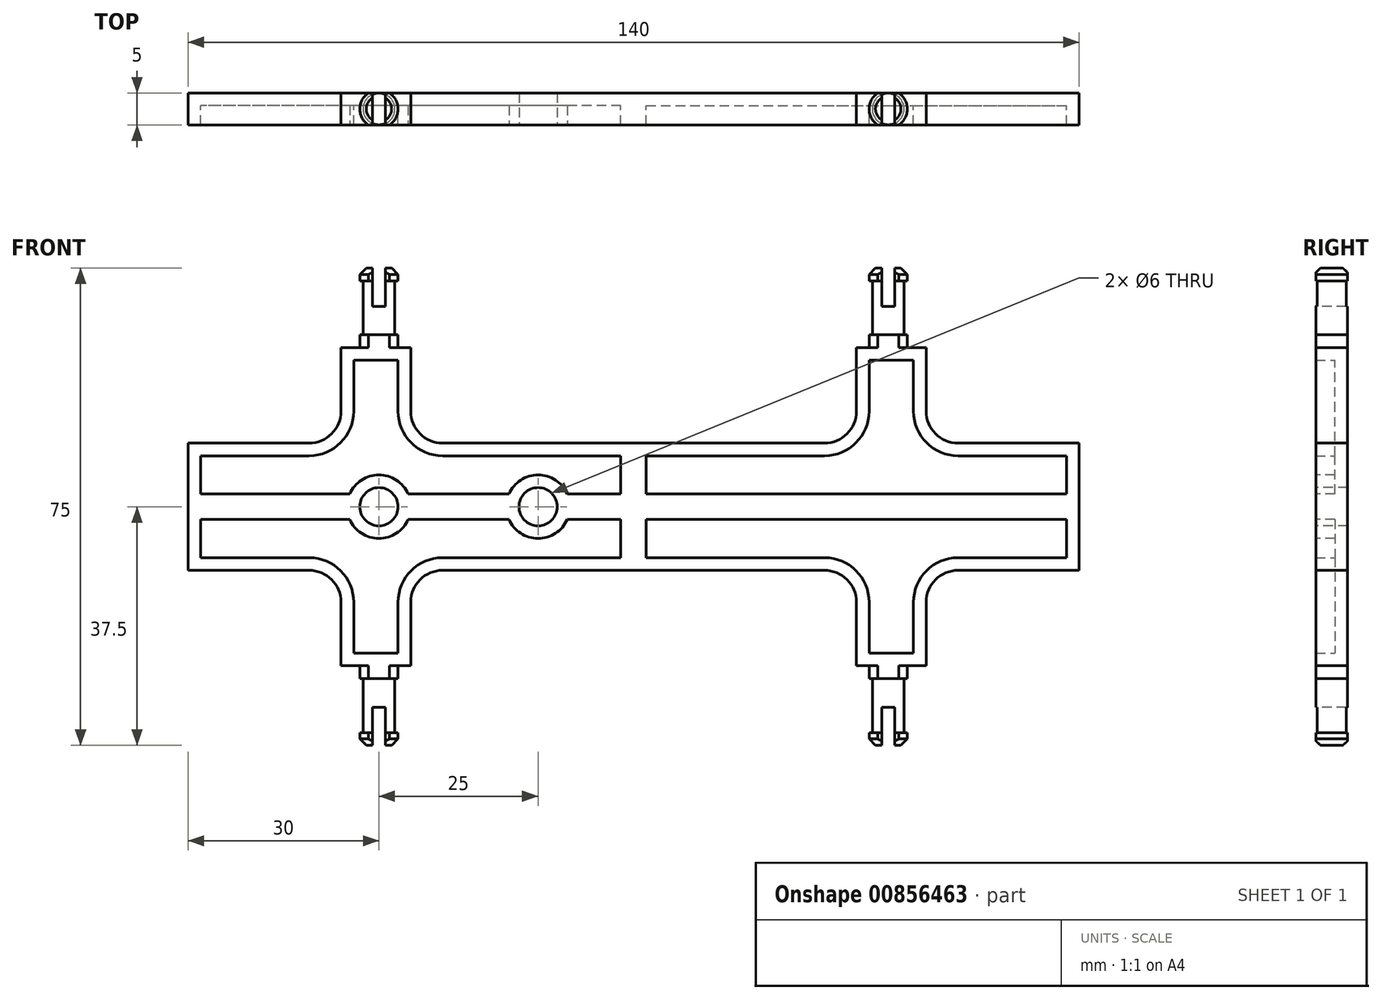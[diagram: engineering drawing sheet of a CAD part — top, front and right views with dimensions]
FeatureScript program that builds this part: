
annotation { "Feature Type Name" : "Feature", "Feature Type Description" : "" }
export const myFeature = defineFeature(function(context is Context, id is Id, definition is map)
    precondition{}
    {
        {
            var Q0;
            Q0=qCreatedBy(makeId("Front.planeOp"),FACE);
            var sketch = newSketch(context, id + "F0", { "sketchPlane" : qUnion([Q0])});
            skLineSegment(sketch, "E0.bottom", {"start": v(0, 0) * mm, "end": v(70, 0) * mm});
            skLineSegment(sketch, "E0.top", {"start": v(0, 10) * mm, "end": v(30, 10) * mm});
            skLineSegment(sketch, "E0.left", {"start": v(0, 0) * mm, "end": v(0, 10) * mm});
            skLineSegment(sketch, "E0.right", {"start": v(70, 0) * mm, "end": v(70, 10) * mm});
            skLineSegment(sketch, "E1.top", {"start": v(35, 25) * mm, "end": v(45.97, 25) * mm});
            skLineSegment(sketch, "E1.left", {"start": v(35, 15) * mm, "end": v(35, 25) * mm});
            skLineSegment(sketch, "E1.right", {"start": v(45.97, 15) * mm, "end": v(45.97, 25) * mm});
            skLineSegment(sketch, "E2.trimOffspring", {"start": v(50.97, 10) * mm, "end": v(70, 10) * mm});
            skPoint(sketch, "E3.visualSharp", {"position": v(35, 10) * mm});
            skArc(sketch, "E3.filletArc", {"start": v(30, 10) * mm, "mid": v(33.54, 11.46) * mm, "end": v(35, 15) * mm});
            skPoint(sketch, "E4.visualSharp", {"position": v(45.97, 10) * mm});
            skArc(sketch, "E4.filletArc", {"start": v(45.97, 15) * mm, "mid": v(47.43, 11.46) * mm, "end": v(50.97, 10) * mm});
            skSolve(sketch);
        }
        {
            var Q0;
            Q0 = qSketchRegion(id + "F0", true);
            extrude(context, id + "F1", {"entities" : qUnion([Q0]), "endBound" : BoundingType.SYMMETRIC, "depth" : 5 * mm, "offsetDistance" : 25 * mm});
        }
        {
            var Q0;
            Q0=makeQuery(id+"F1.opExtrude","CAP_FACE",FACE,{"disambiguationData":[OSD([sQuery(id+"F0.wireOp",EDGE,"E0.bottom"),sQuery(id+"F0.wireOp",EDGE,"E0.top"),sQuery(id+"F0.wireOp",EDGE,"E0.left"),sQuery(id+"F0.wireOp",EDGE,"E0.right"),sQuery(id+"F0.wireOp",EDGE,"E1.top"),sQuery(id+"F0.wireOp",EDGE,"E1.left"),sQuery(id+"F0.wireOp",EDGE,"E1.right"),sQuery(id+"F0.wireOp",EDGE,"E2.trimOffspring"),sQuery(id+"F0.wireOp",EDGE,"E3.filletArc"),sQuery(id+"F0.wireOp",EDGE,"E4.filletArc")])],"isStart":false});
            shell(context, id + "F2", {"entities" : qUnion([Q0]), "thickness" : 2 * mm});
        }
        {
            var Q0;
            Q0=qCreatedBy(makeId("Front.planeOp"),FACE);
            var sketch = newSketch(context, id + "F3", { "sketchPlane" : qUnion([Q0])});
            skLineSegment(sketch, "E5", {"start": v(40, 25) * mm, "end": v(40, 37.5) * mm});
            skLineSegment(sketch, "E6", {"start": v(40, 37.5) * mm, "end": v(37, 37.5) * mm});
            skLineSegment(sketch, "E7", {"start": v(37, 37.5) * mm, "end": v(37, 35.5) * mm});
            skLineSegment(sketch, "E8", {"start": v(37, 35.5) * mm, "end": v(37.5, 35.5) * mm});
            skLineSegment(sketch, "E9", {"start": v(37.5, 35.5) * mm, "end": v(37.5, 27) * mm});
            skLineSegment(sketch, "E10", {"start": v(37.5, 27) * mm, "end": v(37, 27) * mm});
            skLineSegment(sketch, "E11", {"start": v(37, 27) * mm, "end": v(37, 25) * mm});
            skLineSegment(sketch, "E12", {"start": v(37, 25) * mm, "end": v(40, 25) * mm});
            skSolve(sketch);
        }
        {
            var Q0;
            Q0 = qSketchRegion(id + "F3", true);
            var Q1;
            Q1=sQuery(id+"F3.wireOp",EDGE,"E5");
            revolve(context, id + "F4", {"operationType" : NewBodyOperationType.ADD, "surfaceOperationType" : NewSurfaceOperationType.NEW, "entities" : qUnion([Q0]), "axis" : qUnion([Q1]), "revolveType" : RevolveType.FULL});
        }
        {
            var Q0;
            Q0=makeQuery(id+"F4.opRevolve","SWEPT_FACE",FACE,{"disambiguationData":[OSD([sQuery(id+"F3.wireOp",EDGE,"E6")])]});
            chamfer(context, id + "F5", {"entities" : qUnion([Q0]), "width" : 1 * mm, "tangentPropagation" : true});
        }
        {
            var Q0;
            Q0=makeQuery(id+"F4.opRevolve","SWEPT_FACE",FACE,{"disambiguationData":[OSD([sQuery(id+"F3.wireOp",EDGE,"E6")])]});
            var sketch = newSketch(context, id + "F6", { "sketchPlane" : qUnion([Q0])});
            skLineSegment(sketch, "E13.bottom", {"start": v(0, 2.5) * mm, "end": v(75, 2.5) * mm});
            skLineSegment(sketch, "E13.top", {"start": v(0, -2.5) * mm, "end": v(75, -2.5) * mm});
            skLineSegment(sketch, "E13.left", {"start": v(0, 2.5) * mm, "end": v(0, -2.5) * mm});
            skLineSegment(sketch, "E13.right", {"start": v(75, 2.5) * mm, "end": v(75, -2.5) * mm});
            skSolve(sketch);
        }
        {
            var Q0;
            Q0 = qSketchRegion(id + "F6", true);
            extrude(context, id + "F7", {"entities" : qUnion([Q0]), "operationType" : NewBodyOperationType.INTERSECT, "endBound" : BoundingType.THROUGH_ALL, "oppositeDirection" : true, "depth" : 25 * mm, "offsetDistance" : 25 * mm});
        }
        {
            var Q0;
            Q0=makeQuery(id+"F4.opRevolve","SWEPT_FACE",FACE,{"disambiguationData":[OSD([sQuery(id+"F3.wireOp",EDGE,"E6")])]});
            var sketch = newSketch(context, id + "F8", { "sketchPlane" : qUnion([Q0])});
            skLineSegment(sketch, "E14.bottom", {"start": v(39, 3.87) * mm, "end": v(41, 3.87) * mm});
            skLineSegment(sketch, "E14.top", {"start": v(39, -3.44) * mm, "end": v(41, -3.44) * mm});
            skLineSegment(sketch, "E14.left", {"start": v(39, 3.87) * mm, "end": v(39, -3.44) * mm});
            skLineSegment(sketch, "E14.right", {"start": v(41, 3.87) * mm, "end": v(41, -3.44) * mm});
            skSolve(sketch);
        }
        {
            var Q0;
            Q0 = qSketchRegion(id + "F8", true);
            extrude(context, id + "F9", {"entities" : qUnion([Q0]), "operationType" : NewBodyOperationType.REMOVE, "oppositeDirection" : true, "depth" : 6 * mm, "offsetDistance" : 25 * mm});
        }
        {
            var Q0;
            Q0=makeQuery(id+"F1.opExtrude","SWEPT_BODY",BODY,{"disambiguationData":[OSD([sQuery(id+"F0.wireOp",EDGE,"E0.bottom"),sQuery(id+"F0.wireOp",EDGE,"E0.top"),sQuery(id+"F0.wireOp",EDGE,"E0.left"),sQuery(id+"F0.wireOp",EDGE,"E0.right"),sQuery(id+"F0.wireOp",EDGE,"E1.top"),sQuery(id+"F0.wireOp",EDGE,"E1.left"),sQuery(id+"F0.wireOp",EDGE,"E1.right"),sQuery(id+"F0.wireOp",EDGE,"E2.trimOffspring"),sQuery(id+"F0.wireOp",EDGE,"E3.filletArc"),sQuery(id+"F0.wireOp",EDGE,"E4.filletArc")])]});
            var Q1;
            Q1=qCreatedBy(makeId("Top.planeOp"),FACE);
            mirror(context, id + "F10", {"operationType" : NewBodyOperationType.ADD, "entities" : qUnion([Q0]), "mirrorPlane" : qUnion([Q1])});
        }
        {
            var Q0;
            Q0=makeQuery(id+"F1.opExtrude","SWEPT_BODY",BODY,{"disambiguationData":[OSD([sQuery(id+"F0.wireOp",EDGE,"E0.bottom"),sQuery(id+"F0.wireOp",EDGE,"E0.top"),sQuery(id+"F0.wireOp",EDGE,"E0.left"),sQuery(id+"F0.wireOp",EDGE,"E0.right"),sQuery(id+"F0.wireOp",EDGE,"E1.top"),sQuery(id+"F0.wireOp",EDGE,"E1.left"),sQuery(id+"F0.wireOp",EDGE,"E1.right"),sQuery(id+"F0.wireOp",EDGE,"E2.trimOffspring"),sQuery(id+"F0.wireOp",EDGE,"E3.filletArc"),sQuery(id+"F0.wireOp",EDGE,"E4.filletArc")])]});
            var Q1;
            Q1=qCreatedBy(makeId("Right.planeOp"),FACE);
            mirror(context, id + "F11", {"operationType" : NewBodyOperationType.ADD, "entities" : qUnion([Q0]), "mirrorPlane" : qUnion([Q1])});
        }
        {
            var Q0;
            {var subQ0=makeQuery(id+"F7.boolean.opBoolean","MERGE",FACE,{"derivedFrom":[makeQuery(id+"F1.opExtrude","CAP_FACE",FACE,{"disambiguationData":[OSD([sQuery(id+"F0.wireOp",EDGE,"E0.bottom"),sQuery(id+"F0.wireOp",EDGE,"E0.top"),sQuery(id+"F0.wireOp",EDGE,"E0.left"),sQuery(id+"F0.wireOp",EDGE,"E0.right"),sQuery(id+"F0.wireOp",EDGE,"E1.top"),sQuery(id+"F0.wireOp",EDGE,"E1.left"),sQuery(id+"F0.wireOp",EDGE,"E1.right"),sQuery(id+"F0.wireOp",EDGE,"E2.trimOffspring"),sQuery(id+"F0.wireOp",EDGE,"E3.filletArc"),sQuery(id+"F0.wireOp",EDGE,"E4.filletArc")])],"isStart":false})],"fromTools":[makeQuery(id+"F7.boolean.toolComplement.opBoolean","COPY",FACE,{"derivedFrom":makeQuery(id+"F7.opExtrude","SWEPT_FACE",FACE,{"disambiguationData":[OSD([sQuery(id+"F6.wireOp",EDGE,"E13.top")])]})})]});var subQ1=makeQuery(id+"F10.boolean.opBoolean","MERGE",FACE,{"derivedFrom":[subQ0,makeQuery(id+"F10.opPattern","COPY",FACE,{"derivedFrom":subQ0,"instanceName":"1"})]});Q0=makeQuery(id+"F11.boolean.opBoolean","MERGE",FACE,{"derivedFrom":[subQ1,makeQuery(id+"F11.opPattern","COPY",FACE,{"derivedFrom":subQ1,"instanceName":"1"})]});}
            var sketch = newSketch(context, id + "F12", { "sketchPlane" : qUnion([Q0])});
            skCircle(sketch, "E15", {"center": v(-40, 0) * mm, "radius": 5 * mm});
            skCircle(sketch, "E16", {"center": v(-15, 0) * mm, "radius": 5 * mm});
            skSolve(sketch);
        }
        {
            var Q0;
            Q0 = qSketchRegion(id + "F12", true);
            extrude(context, id + "F13", {"entities" : qUnion([Q0]), "operationType" : NewBodyOperationType.ADD, "endBound" : BoundingType.UP_TO_NEXT, "oppositeDirection" : true, "depth" : 25 * mm, "offsetDistance" : 25 * mm});
        }
        {
            var Q0;
            {var subQ0=makeQuery(id+"F7.boolean.opBoolean","MERGE",FACE,{"derivedFrom":[makeQuery(id+"F1.opExtrude","CAP_FACE",FACE,{"disambiguationData":[OSD([sQuery(id+"F0.wireOp",EDGE,"E0.bottom"),sQuery(id+"F0.wireOp",EDGE,"E0.top"),sQuery(id+"F0.wireOp",EDGE,"E0.left"),sQuery(id+"F0.wireOp",EDGE,"E0.right"),sQuery(id+"F0.wireOp",EDGE,"E1.top"),sQuery(id+"F0.wireOp",EDGE,"E1.left"),sQuery(id+"F0.wireOp",EDGE,"E1.right"),sQuery(id+"F0.wireOp",EDGE,"E2.trimOffspring"),sQuery(id+"F0.wireOp",EDGE,"E3.filletArc"),sQuery(id+"F0.wireOp",EDGE,"E4.filletArc")])],"isStart":false})],"fromTools":[makeQuery(id+"F7.boolean.toolComplement.opBoolean","COPY",FACE,{"derivedFrom":makeQuery(id+"F7.opExtrude","SWEPT_FACE",FACE,{"disambiguationData":[OSD([sQuery(id+"F6.wireOp",EDGE,"E13.top")])]})})]});var subQ1=makeQuery(id+"F10.boolean.opBoolean","MERGE",FACE,{"derivedFrom":[subQ0,makeQuery(id+"F10.opPattern","COPY",FACE,{"derivedFrom":subQ0,"instanceName":"1"})]});Q0=makeQuery(id+"F13.boolean.opBoolean","MERGE",FACE,{"derivedFrom":[makeQuery(id+"F11.boolean.opBoolean","MERGE",FACE,{"derivedFrom":[subQ1,makeQuery(id+"F11.opPattern","COPY",FACE,{"derivedFrom":subQ1,"instanceName":"1"})]}),makeQuery(id+"F13.opExtrude","CAP_FACE",FACE,{"disambiguationData":[OSD([sQuery(id+"F12.wireOp",EDGE,"E15")])],"isStart":true}),makeQuery(id+"F13.opExtrude","CAP_FACE",FACE,{"disambiguationData":[OSD([sQuery(id+"F12.wireOp",EDGE,"E16")])],"isStart":true})]});}
            var sketch = newSketch(context, id + "F14", { "sketchPlane" : qUnion([Q0])});
            skPoint(sketch, "E17", {"position": v(-40, 0) * mm});
            skPoint(sketch, "E18", {"position": v(-15, 0) * mm});
            skSolve(sketch);
        }
        {
            var Q0;
            Q0=sQuery(id+"F14.wireOp",VERTEX,"E17");
            var Q1;
            Q1=sQuery(id+"F14.wireOp",VERTEX,"E18");
            var Q2;
            Q2=makeQuery(id+"F1.opExtrude","SWEPT_BODY",BODY,{"disambiguationData":[OSD([sQuery(id+"F0.wireOp",EDGE,"E0.bottom"),sQuery(id+"F0.wireOp",EDGE,"E0.top"),sQuery(id+"F0.wireOp",EDGE,"E0.left"),sQuery(id+"F0.wireOp",EDGE,"E0.right"),sQuery(id+"F0.wireOp",EDGE,"E1.top"),sQuery(id+"F0.wireOp",EDGE,"E1.left"),sQuery(id+"F0.wireOp",EDGE,"E1.right"),sQuery(id+"F0.wireOp",EDGE,"E2.trimOffspring"),sQuery(id+"F0.wireOp",EDGE,"E3.filletArc"),sQuery(id+"F0.wireOp",EDGE,"E4.filletArc")])]});
            hole(context, id + "F15", {"style" : HoleStyle.SIMPLE, "endStyle" : HoleEndStyle.THROUGH, "holeDiameter" : 6 * mm, "majorDiameter" : 5 * mm, "isTappedThrough" : true, "tappedDepth" : 12 * mm, "tapClearance" : 3, "locations" : qUnion([Q0, Q1]), "scope" : qUnion([Q2])});
        }
    });
